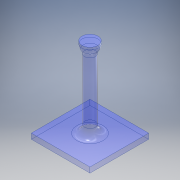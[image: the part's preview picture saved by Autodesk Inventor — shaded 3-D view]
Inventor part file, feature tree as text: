
AUTODESK INVENTOR PART (.ipt)
format: ipt  version: 2017 (Build 210142000, 142)  size: 138,240 bytes
history: native  units: mm
features: sketch x4, extrude x3, fillet x2
ambient origin geometry x8: Origin, YZ Plane, XZ Plane, XY Plane, X Axis, Y Axis, Z Axis, Center Point
bodies: Solid1 (feature_tree)
feature tree (9):
  extrude  "Extrusion1"  Depth=70.0mm TaperAngle=0.0deg
  extrude  "Extrusion2"  Depth=5.0mm TaperAngle=0.0deg
  fillet  "Fillet1"  Radius=7.25mm
  extrude  "Extrusion3"  Depth=55.0mm
  fillet  "Fillet2"  Radius=5.0mm
  sketch  "3D Sketch1"
  sketch  "Sketch1"  dims[d0=10.0mm d1=70.0mm d2=0.0mm]
  sketch  "Sketch2"  dims[d3=15.0mm d4=5.0mm d5=0.0mm d6=7.25mm]
  sketch  "Sketch3"  dims[d7=55.0mm d8=55.0mm d9=5.0mm d10=0.0mm d11=7.25mm]
